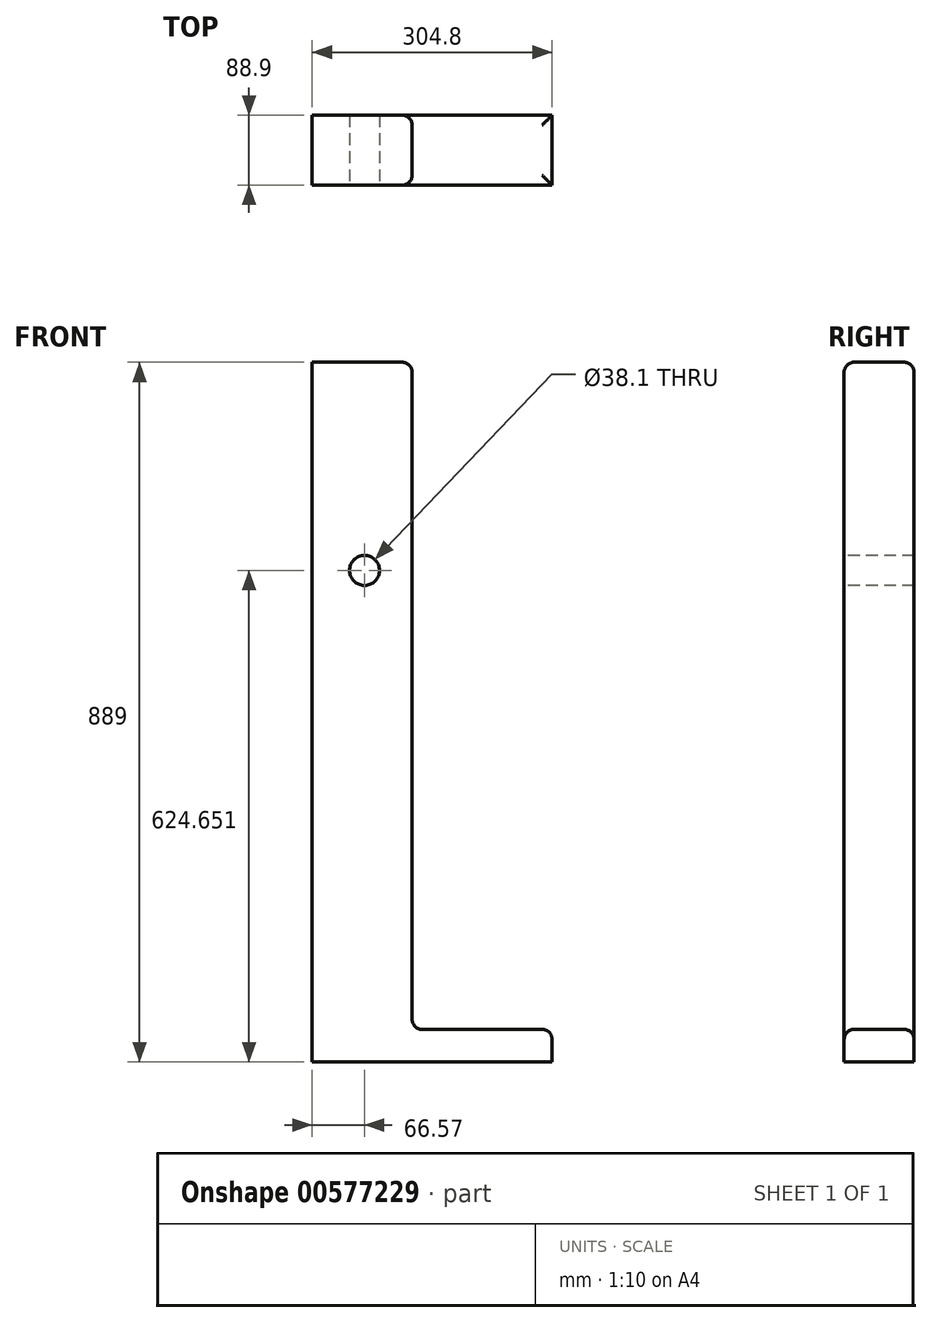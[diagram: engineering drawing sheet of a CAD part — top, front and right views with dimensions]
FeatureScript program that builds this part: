
annotation { "Feature Type Name" : "Feature", "Feature Type Description" : "" }
export const myFeature = defineFeature(function(context is Context, id is Id, definition is map)
    precondition{}
    {
        {
            var Q0;
            Q0=qCreatedBy(makeId("Top.planeOp"),FACE);
            var sketch = newSketch(context, id + "F0", { "sketchPlane" : qUnion([Q0])});
            skLineSegment(sketch, "E0.bottom", {"start": v(-66.57, 55.47) * mm, "end": v(60.43, 55.47) * mm});
            skLineSegment(sketch, "E0.top", {"start": v(-66.57, -33.43) * mm, "end": v(60.43, -33.43) * mm});
            skLineSegment(sketch, "E0.left", {"start": v(-66.57, 55.47) * mm, "end": v(-66.57, -33.43) * mm});
            skLineSegment(sketch, "E0.right", {"start": v(60.43, 55.47) * mm, "end": v(60.43, -33.43) * mm});
            skSolve(sketch);
        }
        {
            var Q0;
            Q0=makeQuery(id+"F0.imprint","IMPRINT",FACE,{"disambiguationData":[TD([[makeQuery(id+"F0.imprint","IMPRINT",EDGE,{"derivedFrom":sQuery(id+"F0.wireOp",EDGE,"E0.bottom")}),-1.0]])]});
            extrude(context, id + "F1", {"entities" : qUnion([Q0]), "depth" : 889 * mm, "offsetDistance" : 25.4 * mm});
        }
        {
            var Q0;
            Q0=makeQuery(id+"F1.opExtrude","SWEPT_FACE",FACE,{"disambiguationData":[OSD([sQuery(id+"F0.wireOp",EDGE,"E0.right")])]});
            var sketch = newSketch(context, id + "F2", { "sketchPlane" : qUnion([Q0])});
            skLineSegment(sketch, "E1.bottom", {"start": v(-33.43, 0) * mm, "end": v(55.47, 0) * mm});
            skLineSegment(sketch, "E1.top", {"start": v(-33.43, 41.55) * mm, "end": v(55.47, 41.55) * mm});
            skLineSegment(sketch, "E1.left", {"start": v(-33.43, 0) * mm, "end": v(-33.43, 41.55) * mm});
            skLineSegment(sketch, "E1.right", {"start": v(55.47, 0) * mm, "end": v(55.47, 41.55) * mm});
            skSolve(sketch);
        }
        {
            var Q0;
            Q0 = qSketchRegion(id + "F2", true);
            extrude(context, id + "F3", {"entities" : qUnion([Q0]), "operationType" : NewBodyOperationType.ADD, "depth" : 177.8 * mm, "offsetDistance" : 25.4 * mm});
        }
        {
            var Q0;
            Q0=makeQuery(id+"F1.opExtrude","CAP_EDGE",EDGE,{"disambiguationData":[OSD([sQuery(id+"F0.wireOp",EDGE,"E0.bottom")])],"isStart":false});
            fillet(context, id + "F4", {"entities" : qUnion([Q0]), "radius" : 12.7 * mm, "tangentPropagation" : true, "allowEdgeOverflow" : false});
        }
        {
            var Q0;
            Q0=makeQuery(id+"F3.boolean.opBoolean","MERGE",FACE,{"derivedFrom":[makeQuery(id+"F1.opExtrude","SWEPT_FACE",FACE,{"disambiguationData":[OSD([sQuery(id+"F0.wireOp",EDGE,"E0.top")])]}),makeQuery(id+"F3.opExtrude","SWEPT_FACE",FACE,{"disambiguationData":[OSD([sQuery(id+"F2.wireOp",EDGE,"E1.left")])]})]});
            var sketch = newSketch(context, id + "F5", { "sketchPlane" : qUnion([Q0])});
            skCircle(sketch, "E2", {"center": v(0, 624.65) * mm, "radius": 19.05 * mm});
            skSolve(sketch);
        }
        {
            var Q0;
            Q0 = qSketchRegion(id + "F5", true);
            extrude(context, id + "F6", {"entities" : qUnion([Q0]), "operationType" : NewBodyOperationType.REMOVE, "oppositeDirection" : true, "depth" : 127 * mm, "offsetDistance" : 25.4 * mm});
        }
        {
            var Q0;
            Q0=makeQuery(id+"F1.opExtrude","CAP_EDGE",EDGE,{"disambiguationData":[OSD([sQuery(id+"F0.wireOp",EDGE,"E0.top")])],"isStart":false});
            var Q1;
            Q1=makeQuery(id+"F1.opExtrude","SWEPT_EDGE",EDGE,{"disambiguationData":[OSD([sQuery(id+"F0.wireOp",EDGE,"E0.top"),sQuery(id+"F0.wireOp",EDGE,"E0.right")])]});
            var Q2;
            Q2=makeQuery(id+"F1.opExtrude","SWEPT_EDGE",EDGE,{"disambiguationData":[OSD([sQuery(id+"F0.wireOp",EDGE,"E0.bottom"),sQuery(id+"F0.wireOp",EDGE,"E0.right")])]});
            var Q3;
            Q3=makeQuery(id+"F3.opExtrude","SWEPT_FACE",FACE,{"disambiguationData":[OSD([sQuery(id+"F2.wireOp",EDGE,"E1.top")])]});
            fillet(context, id + "F7", {"entities" : qUnion([Q0, Q1, Q2, Q3]), "radius" : 12.7 * mm, "tangentPropagation" : true, "allowEdgeOverflow" : false});
        }
    });
